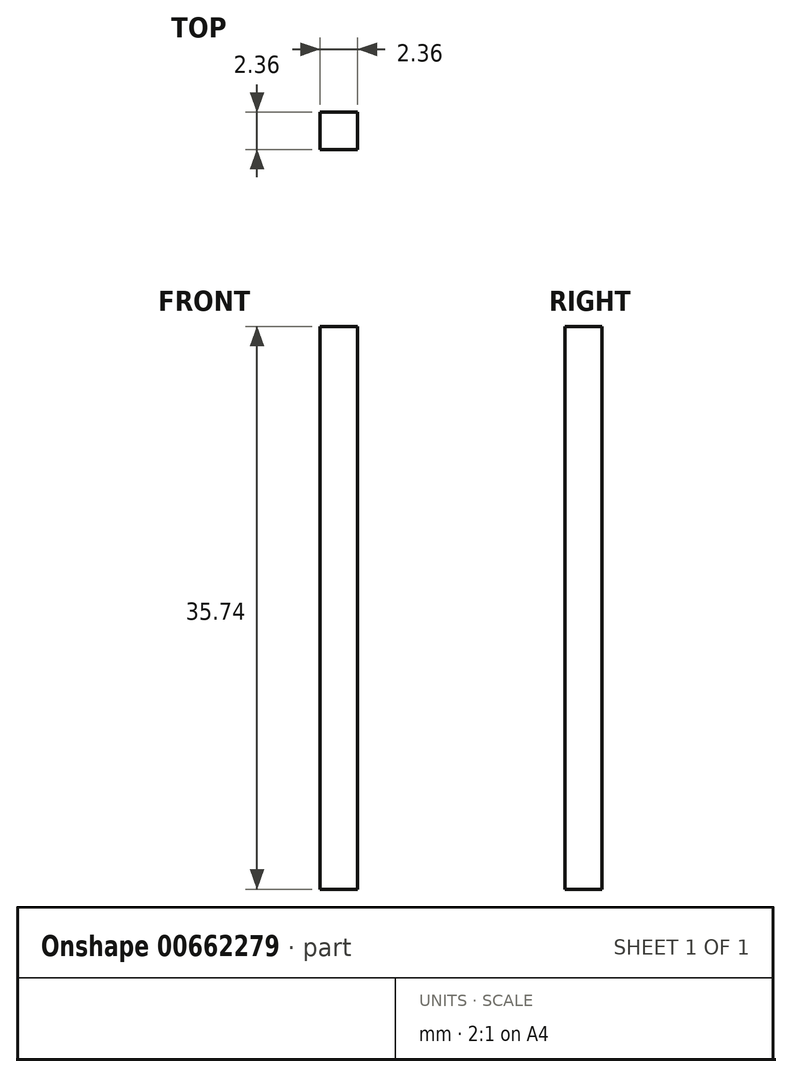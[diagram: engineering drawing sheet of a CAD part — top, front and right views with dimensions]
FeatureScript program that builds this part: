
annotation { "Feature Type Name" : "Feature", "Feature Type Description" : "" }
export const myFeature = defineFeature(function(context is Context, id is Id, definition is map)
    precondition{}
    {
        {
            var Q0;
            Q0=qCreatedBy(makeId("Front.planeOp"),FACE);
            var sketch = newSketch(context, id + "F0", { "sketchPlane" : qUnion([Q0])});
            skLineSegment(sketch, "E0.bottom", {"start": v(38.1, -38.1) * mm, "end": v(-38.1, -38.1) * mm});
            skLineSegment(sketch, "E0.top", {"start": v(38.1, 38.1) * mm, "end": v(-38.1, 38.1) * mm});
            skLineSegment(sketch, "E0.left", {"start": v(38.1, -38.1) * mm, "end": v(38.1, 38.1) * mm});
            skLineSegment(sketch, "E0.right", {"start": v(-38.1, -38.1) * mm, "end": v(-38.1, 38.1) * mm});
            skPoint(sketch, "E0.middle", {"position": v(0, 0) * mm});
            skSolve(sketch);
        }
        {
            var Q0;
            Q0=makeQuery(id+"F0.imprint","IMPRINT",FACE,{"disambiguationData":[TD([[makeQuery(id+"F0.imprint","IMPRINT",EDGE,{"derivedFrom":sQuery(id+"F0.wireOp",EDGE,"E0.bottom")}),-1.0]])]});
            extrude(context, id + "F1", {"entities" : qUnion([Q0]), "depth" : 2.36 * mm, "offsetDistance" : 25.4 * mm});
        }
        {
            var Q0;
            Q0=makeQuery(id+"F1.opExtrude","CAP_FACE",FACE,{"disambiguationData":[OSD([sQuery(id+"F0.wireOp",EDGE,"E0.bottom"),sQuery(id+"F0.wireOp",EDGE,"E0.top"),sQuery(id+"F0.wireOp",EDGE,"E0.left"),sQuery(id+"F0.wireOp",EDGE,"E0.right")])],"isStart":false});
            var sketch = newSketch(context, id + "F2", { "sketchPlane" : qUnion([Q0])});
            skLineSegment(sketch, "E1.bottom", {"start": v(-38.1, 38.1) * mm, "end": v(-12.7, 38.1) * mm});
            skLineSegment(sketch, "E1.top", {"start": v(-38.1, 35.74) * mm, "end": v(-12.7, 35.74) * mm});
            skLineSegment(sketch, "E1.left", {"start": v(-38.1, 38.1) * mm, "end": v(-38.1, 35.74) * mm});
            skLineSegment(sketch, "E1.right", {"start": v(-12.7, 38.1) * mm, "end": v(-12.7, 35.74) * mm});
            skLineSegment(sketch, "E2.bottom", {"start": v(12.7, 38.1) * mm, "end": v(38.1, 38.1) * mm});
            skLineSegment(sketch, "E2.top", {"start": v(12.7, 35.74) * mm, "end": v(38.1, 35.74) * mm});
            skLineSegment(sketch, "E2.left", {"start": v(12.7, 38.1) * mm, "end": v(12.7, 35.74) * mm});
            skLineSegment(sketch, "E2.right", {"start": v(38.1, 38.1) * mm, "end": v(38.1, 35.74) * mm});
            skSolve(sketch);
        }
        {
            var Q0;
            Q0 = qSketchRegion(id + "F2", true);
            extrude(context, id + "F3", {"entities" : qUnion([Q0]), "operationType" : NewBodyOperationType.REMOVE, "endBound" : BoundingType.THROUGH_ALL, "oppositeDirection" : true, "depth" : 25.4 * mm, "offsetDistance" : 25.4 * mm});
        }
        {
            var Q0;
            Q0=makeQuery(id+"F1.opExtrude","CAP_FACE",FACE,{"disambiguationData":[OSD([sQuery(id+"F0.wireOp",EDGE,"E0.bottom"),sQuery(id+"F0.wireOp",EDGE,"E0.top"),sQuery(id+"F0.wireOp",EDGE,"E0.left"),sQuery(id+"F0.wireOp",EDGE,"E0.right")])],"isStart":false});
            var sketch = newSketch(context, id + "F4", { "sketchPlane" : qUnion([Q0])});
            skLineSegment(sketch, "E3.bottom", {"start": v(38.1, -35.74) * mm, "end": v(35.74, -35.74) * mm});
            skLineSegment(sketch, "E3.top", {"start": v(38.1, 0) * mm, "end": v(35.74, 0) * mm});
            skLineSegment(sketch, "E3.left", {"start": v(38.1, -35.74) * mm, "end": v(38.1, 0) * mm});
            skLineSegment(sketch, "E3.right", {"start": v(35.74, -35.74) * mm, "end": v(35.74, 0) * mm});
            skLineSegment(sketch, "E4.bottom", {"start": v(-38.1, 35.74) * mm, "end": v(-35.74, 35.74) * mm});
            skLineSegment(sketch, "E4.top", {"start": v(-38.1, 0) * mm, "end": v(-35.74, 0) * mm});
            skLineSegment(sketch, "E4.left", {"start": v(-38.1, 35.74) * mm, "end": v(-38.1, 0) * mm});
            skLineSegment(sketch, "E4.right", {"start": v(-35.74, 35.74) * mm, "end": v(-35.74, 0) * mm});
            skSolve(sketch);
        }
        {
            var Q0;
            Q0=makeQuery(id+"F4.imprint","IMPRINT",FACE,{"disambiguationData":[TD([[makeQuery(id+"F4.imprint","IMPRINT",EDGE,{"derivedFrom":sQuery(id+"F4.wireOp",EDGE,"E4.bottom")}),-1.0]])]});
            var Q1;
            Q1=makeQuery(id+"F4.imprint","IMPRINT",FACE,{"disambiguationData":[TD([[makeQuery(id+"F4.imprint","IMPRINT",EDGE,{"derivedFrom":sQuery(id+"F4.wireOp",EDGE,"E3.bottom")}),1.0]])]});
            extrude(context, id + "F5", {"entities" : qUnion([Q0, Q1]), "operationType" : NewBodyOperationType.REMOVE, "oppositeDirection" : true, "depth" : 25.4 * mm, "offsetDistance" : 25.4 * mm});
        }
        {
            var Q0;
            Q0=makeQuery(id+"F1.opExtrude","CAP_FACE",FACE,{"disambiguationData":[OSD([sQuery(id+"F0.wireOp",EDGE,"E0.bottom"),sQuery(id+"F0.wireOp",EDGE,"E0.top"),sQuery(id+"F0.wireOp",EDGE,"E0.left"),sQuery(id+"F0.wireOp",EDGE,"E0.right")])],"isStart":false});
            var sketch = newSketch(context, id + "F6", { "sketchPlane" : qUnion([Q0])});
            skLineSegment(sketch, "E5.bottom", {"start": v(6.35, 19.09) * mm, "end": v(-6.35, 19.09) * mm});
            skLineSegment(sketch, "E5.top", {"start": v(6.35, 21.37) * mm, "end": v(-6.35, 21.37) * mm});
            skLineSegment(sketch, "E5.left", {"start": v(6.35, 19.09) * mm, "end": v(6.35, 21.37) * mm});
            skLineSegment(sketch, "E5.right", {"start": v(-6.35, 19.09) * mm, "end": v(-6.35, 21.37) * mm});
            skPoint(sketch, "E5.middle", {"position": v(0, 20.23) * mm});
            skLineSegment(sketch, "E6.bottom", {"start": v(6.35, 6.35) * mm, "end": v(-6.35, 6.35) * mm});
            skLineSegment(sketch, "E6.top", {"start": v(6.35, 8.71) * mm, "end": v(-6.35, 8.71) * mm});
            skLineSegment(sketch, "E6.left", {"start": v(6.35, 6.35) * mm, "end": v(6.35, 8.71) * mm});
            skLineSegment(sketch, "E6.right", {"start": v(-6.35, 6.35) * mm, "end": v(-6.35, 8.71) * mm});
            skPoint(sketch, "E6.middle", {"position": v(0, 7.53) * mm});
            skSolve(sketch);
        }
        {
            var Q0;
            Q0=makeQuery(id+"F6.imprint","IMPRINT",FACE,{"disambiguationData":[TD([[makeQuery(id+"F6.imprint","IMPRINT",EDGE,{"derivedFrom":sQuery(id+"F6.wireOp",EDGE,"E5.bottom")}),-1.0]])]});
            var Q1;
            Q1=makeQuery(id+"F6.imprint","IMPRINT",FACE,{"disambiguationData":[TD([[makeQuery(id+"F6.imprint","IMPRINT",EDGE,{"derivedFrom":sQuery(id+"F6.wireOp",EDGE,"E6.bottom")}),-1.0]])]});
            extrude(context, id + "F7", {"entities" : qUnion([Q0, Q1]), "operationType" : NewBodyOperationType.REMOVE, "oppositeDirection" : true, "depth" : 25.4 * mm, "offsetDistance" : 25.4 * mm});
        }
    });
